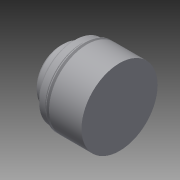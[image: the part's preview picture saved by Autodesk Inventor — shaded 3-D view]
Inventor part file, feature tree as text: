
AUTODESK INVENTOR PART (.ipt)
format: ipt  version: 2014 SP2 (Build 180246200, 246)  size: 187,392 bytes
history: native  units: in
note: dims shown in document units (in); Inventor stores cm internally (conversion verified against a paired STEP export)
features: other x84, revolve x3, sketch x3
ambient origin geometry x8: Origin, YZ Plane, XZ Plane, XY Plane, X Axis, Y Axis, Z Axis, Center Point
bodies: Solid1 (feature_tree)
feature tree (90):
  revolve  "Revolution1"  Angle=360.0deg
  revolve  "Revolution2"  [1 undecoded]
  revolve  "Revolution3"  [1 undecoded]
  other  "lovra_XY"
  other  "lovra_YZ"
  other  "lovra_ZX"
  other  "lovra_X"
  other  "lovra_Y"
  other  "lovra_Z"
  other  "lovra_Center"
  other  "lovra1_XY"
  other  "lovra1_YZ"
  other  "lovra1_ZX"
  other  "lovra1_X"
  other  "lovra1_Y"
  other  "lovra1_Z"
  other  "lovra1_Center"
  other  "lovra2_XY"
  other  "lovra2_YZ"
  other  "lovra2_ZX"
  other  "lovra2_X"
  other  "lovra2_Y"
  other  "lovra2_Z"
  other  "lovra2_Center"
  other  "lovra21_XY"
  other  "lovra21_YZ"
  other  "lovra21_ZX"
  other  "lovra21_X"
  other  "lovra21_Y"
  other  "lovra21_Z"
  other  "lovra21_Center"
  other  "lovra22_XY"
  other  "lovra22_YZ"
  other  "lovra22_ZX"
  other  "lovra22_X"
  other  "lovra22_Y"
  other  "lovra22_Z"
  other  "lovra22_Center"
  other  "lovra3_XY"
  other  "lovra3_YZ"
  other  "lovra3_ZX"
  other  "lovra3_X"
  other  "lovra3_Y"
  other  "lovra3_Z"
  other  "lovra3_Center"
  other  "olen_XY"
  other  "olen_YZ"
  other  "olen_ZX"
  other  "olen_X"
  other  "olen_Y"
  other  "olen_Z"
  other  "olen_Center"
  other  "to_mounting_bracket_XY"
  other  "to_mounting_bracket_YZ"
  other  "to_mounting_bracket_ZX"
  other  "to_mounting_bracket_X"
  other  "to_mounting_bracket_Y"
  other  "to_mounting_bracket_Z"
  other  "to_mounting_bracket_Center"
  other  "to_nut_XY"
  other  "to_nut_YZ"
  other  "to_nut_ZX"
  other  "to_nut_X"
  other  "to_nut_Y"
  other  "to_nut_Z"
  other  "to_nut_Center"
  other  "to_pin_XY"
  other  "to_pin_YZ"
  other  "to_pin_ZX"
  other  "to_pin_X"
  other  "to_pin_Y"
  other  "to_pin_Z"
  other  "to_pin_Center"
  other  "to_screw_XY"
  other  "to_screw_YZ"
  other  "to_screw_ZX"
  other  "to_screw_X"
  other  "to_screw_Y"
  other  "to_screw_Z"
  other  "to_screw_Center"
  other  "to_tube_XY"
  other  "to_tube_YZ"
  other  "to_tube_ZX"
  other  "to_tube_X"
  other  "to_tube_Y"
  other  "to_tube_Z"
  other  "to_tube_Center"
  sketch  "Sketch_1"  dims[d0=360.0deg d1=360.0deg]
  sketch  "Sketch_24"  dims[d2=360.0deg]
  sketch  "Sketch_26"  dims[d3=0.0in d4=0.0in d5=0.0in d6=0.0in d7=0.0in]
note: 2 required parameter values undecoded (feature->parameter linkage not recoverable at this tier; creation-order binding heuristic only, values carry confidence <= 0.55)
